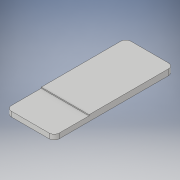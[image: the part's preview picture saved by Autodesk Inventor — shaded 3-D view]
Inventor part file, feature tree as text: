
AUTODESK INVENTOR PART (.ipt)
format: ipt  version: 2019 (Build 230136000, 136)  size: 113,664 bytes
history: native  units: in
note: dims shown in document units (in); Inventor stores cm internally (conversion verified against a paired STEP export)
features: extrude x2, sketch x2
ambient origin geometry x8: Origin, YZ Plane, XZ Plane, XY Plane, X Axis, Y Axis, Z Axis, Center Point
bodies: Solid1 (feature_tree)
feature tree (4):
  extrude  "Extrusion1"  Depth=1.2in
  extrude  "Extrusion2"  Depth=0.06in TaperAngle=0.0deg
  sketch  "Sketch1"  dims[d0=0.48in d1=1.2in]
  sketch  "Sketch2"  dims[d2=0.05in d3=0.06in d4=0.0in d5=0.35in d6=0.48in d7=0.38in d8=0.01in d9=0.0in]
